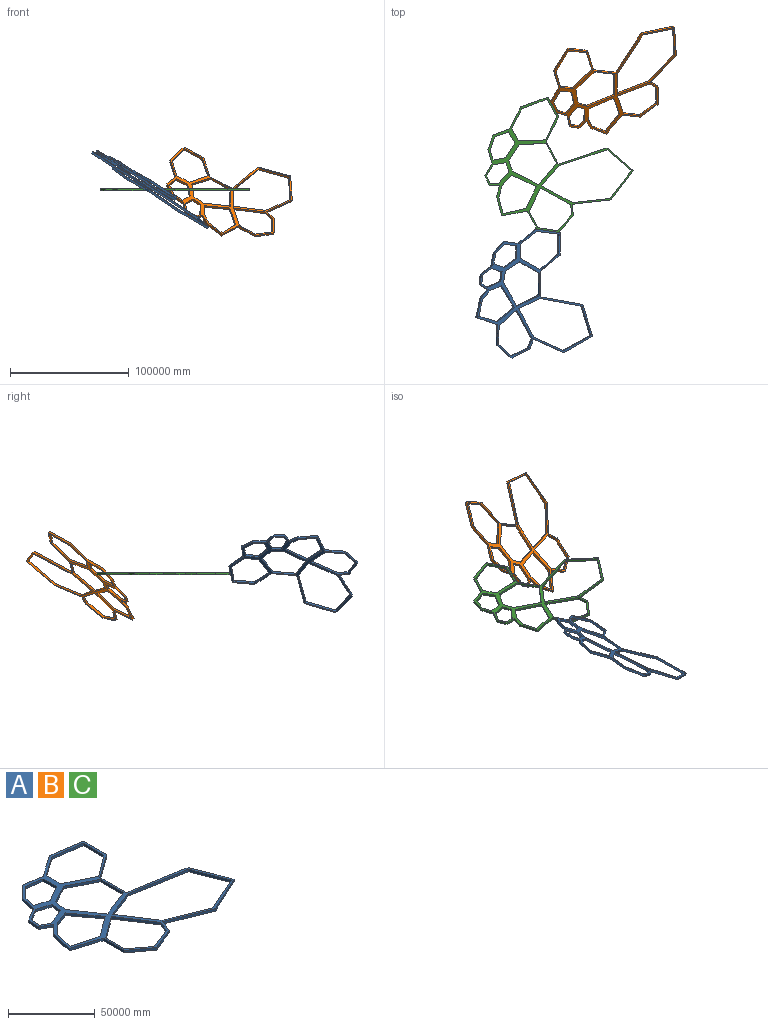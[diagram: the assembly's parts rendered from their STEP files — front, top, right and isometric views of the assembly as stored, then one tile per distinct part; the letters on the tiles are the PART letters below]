
ASSEMBLY  parts=3 mates=3
PART A: 70 faces, bbox 115961.1x108371.6x1778 mm
  f0: plane 20674.97x10033.87mm, normal (0.44,0.9,0), area 40860467.1mm2, adj f1,f67,f68,f69
  f1: plane 11840.58x1778mm, normal (1,0.01,0), area 21053263mm2, adj f0,f2,f68,f69
  f2: plane 15151.22x10634.05mm, normal (0.57,-0.82,0), area 32911847.7mm2, adj f1,f3,f68,f69
  f3: plane 22747.53x2833.86mm, normal (-0.12,-0.99,0), area 40757755.1mm2, adj f2,f4,f68,f69
  f4: plane 16872.15x1778mm, normal (-1,0,0), area 29998683.4mm2, adj f3,f67,f68,f69
  f5: plane 10151.86x3271.69mm, normal (0.31,0.95,0), area 18964210mm2, adj f6,f60,f68,f69
  f6: plane 8570.71x1778mm, normal (0.98,-0.19,0), area 15524181.8mm2, adj f5,f7,f68,f69
  f7: plane 8485.2x7986.07mm, normal (0.69,-0.73,0), area 20717767.2mm2, adj f6,f8,f68,f69
  f8: plane 12235.14x1778mm, normal (-0.14,-0.99,0), area 21974942.5mm2, adj f7,f9,f68,f69
  f9: plane 10643.29x1778mm, normal (-1,-0.04,0), area 18936243.5mm2, adj f8,f60,f68,f69
  f10: plane 7883.51x1778mm, normal (-0.99,0.13,0), area 14141587.9mm2, adj f11,f61,f68,f69
  f11: plane 12845.52x4876.05mm, normal (-0.35,0.93,0), area 24429432.9mm2, adj f10,f12,f68,f69
  f12: plane 5940.56x3208.77mm, normal (0.48,0.88,0), area 12004654.6mm2, adj f11,f13,f68,f69
  f13: plane 7261.13x1778mm, normal (1,-0.07,0), area 12940754.9mm2, adj f12,f14,f68,f69
  f14: plane 9081.31x5596.05mm, normal (0.52,-0.85,0), area 18966015.4mm2, adj f13,f61,f68,f69
  f15: plane 19009.12x5194.63mm, normal (0.26,0.96,0), area 35037459mm2, adj f16,f62,f68,f69
  f16: plane 13664.28x3316.02mm, normal (0.97,-0.24,0), area 25000255.9mm2, adj f15,f17,f68,f69
  f17: plane 7359.82x6968.72mm, normal (0.73,-0.69,0), area 18021063.9mm2, adj f16,f18,f68,f69
  f18: plane 11260.89x4274.54mm, normal (0.35,-0.93,0), area 21415809.9mm2, adj f17,f19,f68,f69
  f19: plane 18558.05x13668.38mm, normal (-0.81,-0.59,0), area 40979945.3mm2, adj f18,f62,f68,f69
  f20: plane 25076.21x9518.72mm, normal (-0.93,-0.35,0), area 47689599.9mm2, adj f21,f63,f68,f69
  f21: plane 27035x11967.49mm, normal (-0.4,0.91,0), area 52567262.9mm2, adj f20,f22,f68,f69
  f22: plane 29445.37x11874.94mm, normal (0.37,0.93,0), area 56450982.9mm2, adj f21,f23,f68,f69
  f23: plane 24532.2x16045.52mm, normal (0.84,0.55,0), area 52119596.9mm2, adj f22,f24,f68,f69
  f24: plane 21280.69x8144.1mm, normal (0.36,-0.93,0), area 40513208mm2, adj f23,f63,f68,f69
  f25: plane 16591.64x6298.05mm, normal (-0.35,0.93,0), area 31553755mm2, adj f26,f64,f68,f69
  f26: plane 13471.29x10263.18mm, normal (0.61,0.8,0), area 30111176.7mm2, adj f25,f27,f68,f69
  f27: plane 15572.16x1778mm, normal (1,0,0), area 27687598.5mm2, adj f26,f28,f68,f69
  f28: plane 17307.6x12747.39mm, normal (0.59,-0.81,0), area 38218685.6mm2, adj f27,f29,f68,f69
  f29: plane 24367.24x15937.63mm, normal (-0.84,-0.55,0), area 51769125.6mm2, adj f28,f64,f68,f69
  f30: plane 20395.5x13948.47mm, normal (0.83,0.56,0), area 43932665.1mm2, adj f31,f65,f68,f69
  f31: plane 9332.29x1778mm, normal (0.99,-0.17,0), area 16835702.1mm2, adj f30,f32,f68,f69
  f32: plane 14215.05x7748.61mm, normal (0.48,-0.88,0), area 28785400mm2, adj f31,f33,f68,f69
  f33: plane 19961.6x10179.53mm, normal (-0.45,-0.89,0), area 39840229.8mm2, adj f32,f34,f68,f69
  f34: plane 18759.07x1778mm, normal (-1,0,0), area 33353619.7mm2, adj f33,f65,f68,f69
  f35: plane 11640.28x2263.58mm, normal (-0.98,0.19,0), area 21084110.9mm2, adj f36,f66,f68,f69
  f36: plane 10353.77x6380.16mm, normal (-0.52,0.85,0), area 21623516.2mm2, adj f35,f37,f68,f69
  f37: plane 8954.62x1778mm, normal (-1,0.07,0), area 15958890.3mm2, adj f36,f38,f68,f69
  f38: plane 7667.39x4141.51mm, normal (-0.48,-0.88,0), area 15494222.9mm2, adj f37,f39,f68,f69
  f39: plane 6886.57x6520.61mm, normal (-0.73,0.69,0), area 16862271.7mm2, adj f38,f40,f68,f69
  f40: plane 16440.02x3989.63mm, normal (-0.97,0.24,0), area 30078758.9mm2, adj f39,f41,f68,f69
  f41: plane 21003.93x6687.22mm, normal (-0.3,-0.95,0), area 39192058.8mm2, adj f40,f42,f68,f69
  f42: plane 17146.61x1778mm, normal (-1,0,0), area 30486679.8mm2, adj f41,f43,f68,f69
  f43: plane 15051.31x11158.47mm, normal (-0.6,-0.8,0), area 33313347.7mm2, adj f42,f44,f68,f69
  f44: plane 17460.04x6828.43mm, normal (0.36,-0.93,0), area 33333603.7mm2, adj f43,f45,f68,f69
  f45: plane 8846x3512.38mm, normal (0.93,-0.37,0), area 16922659.8mm2, adj f44,f46,f68,f69
  f46: plane 30708.58x12193.12mm, normal (-0.37,-0.93,0), area 58746400.2mm2, adj f45,f47,f68,f69
  f47: plane 28224.81x13096.31mm, normal (0.42,-0.91,0), area 55322752.1mm2, adj f46,f48,f68,f69
  f48: plane 1778x1723.39mm, normal (0.82,0.57,0), area 3737501.6mm2, adj f47,f49,f68,f69
  f49: plane 1778x585.96mm, normal (-0.24,-0.97,0), area 1073864.2mm2, adj f48,f50,f68,f69
  f50: plane 25294.09x9906.85mm, normal (0.93,0.36,0), area 48299346.9mm2, adj f49,f51,f68,f69
  f51: plane 1778x1487.19mm, normal (0.17,0.99,0), area 2682931.3mm2, adj f50,f52,f68,f69
  f52: plane 1778x184.43mm, normal (0.78,-0.62,0), area 419043.8mm2, adj f51,f53,f68,f69
  f53: plane 41549.93x7135.47mm, normal (0.17,0.99,0), area 74957231.9mm2, adj f52,f54,f68,f69
  f54: plane 21337.95x1778mm, normal (1,0,0), area 37938878.9mm2, adj f53,f55,f68,f69
  f55: plane 19012.56x13509.67mm, normal (0.58,-0.82,0), area 41469298.1mm2, adj f54,f56,f68,f69
  f56: plane 18892.37x1778mm, normal (1,0,0), area 33590637.6mm2, adj f55,f57,f68,f69
  f57: plane 24208.82x3607.59mm, normal (0.15,0.99,0), area 43518586.2mm2, adj f56,f58,f68,f69
  f58: plane 16970.32x11910.8mm, normal (-0.57,0.82,0), area 36863345.5mm2, adj f57,f59,f68,f69
  f59: plane 14620.23x2088.6mm, normal (0.14,0.99,0), area 26258680.5mm2, adj f58,f66,f68,f69
  f60: plane 12621.79x7437.31mm, normal (-0.51,0.86,0), area 26047738.2mm2, adj f5,f9,f68,f69
  f61: plane 10259.51x3306.38mm, normal (-0.31,-0.95,0), area 19165296.4mm2, adj f10,f14,f68,f69
  f62: plane 16204.88x11935.22mm, normal (-0.59,0.81,0), area 35783659.9mm2, adj f15,f19,f68,f69
  f63: plane 41726.49x7507.53mm, normal (-0.18,-0.98,0), area 75380964.6mm2, adj f20,f24,f68,f69
  f64: plane 7917.45x3254.4mm, normal (-0.92,0.38,0), area 15220043.4mm2, adj f25,f29,f68,f69
  f65: plane 21830.83x8537.8mm, normal (-0.36,0.93,0), area 41678045.8mm2, adj f30,f34,f68,f69
  f66: plane 9683.53x9113.91mm, normal (-0.69,0.73,0), area 23643657.3mm2, adj f35,f59,f68,f69
  f67: plane 17126.5x12802.49mm, normal (-0.6,0.8,0), area 38018478.2mm2, adj f0,f4,f68,f69
  f68: plane 115961.05x108371.57mm, normal (0,0,1), area 1207070154.6mm2, adj f0,f1,f2,f3,f4,f5,f6,f7
  f69: plane 115961.05x108371.57mm, normal (0,0,-1), area 1207070154.6mm2, adj f0,f1,f2,f3,f4,f5,f6,f7
PART B: same geometry as A
PART C: same geometry as A
PLACE A rot(axis=(0.15,0.99,0),32.8deg) t=(136448.46,86367.58,968.11)mm
PLACE B rot(axis=(0.54,-0.09,0.84),84.8deg) t=(214544.4,236779.88,-37746.01)mm
PLACE C rot(axis=(0,0,1),28.1deg) t=(147494.85,178493.59,-21253.18)mm
MATE parallel B.f66 <-> C.f56  axis (-0.88,-0.47,0) through (183510.55,239638.27,-20364.18)mm
MATE parallel C.f43 <-> A.f57  axis (-0.15,-0.99,0) through (178956.43,135502.01,-20364.18)mm
MATE parallel B.f57 <-> A.f40  axis (-0.82,0.21,0.54) through (189731.7,279198.89,9805.46)mm
